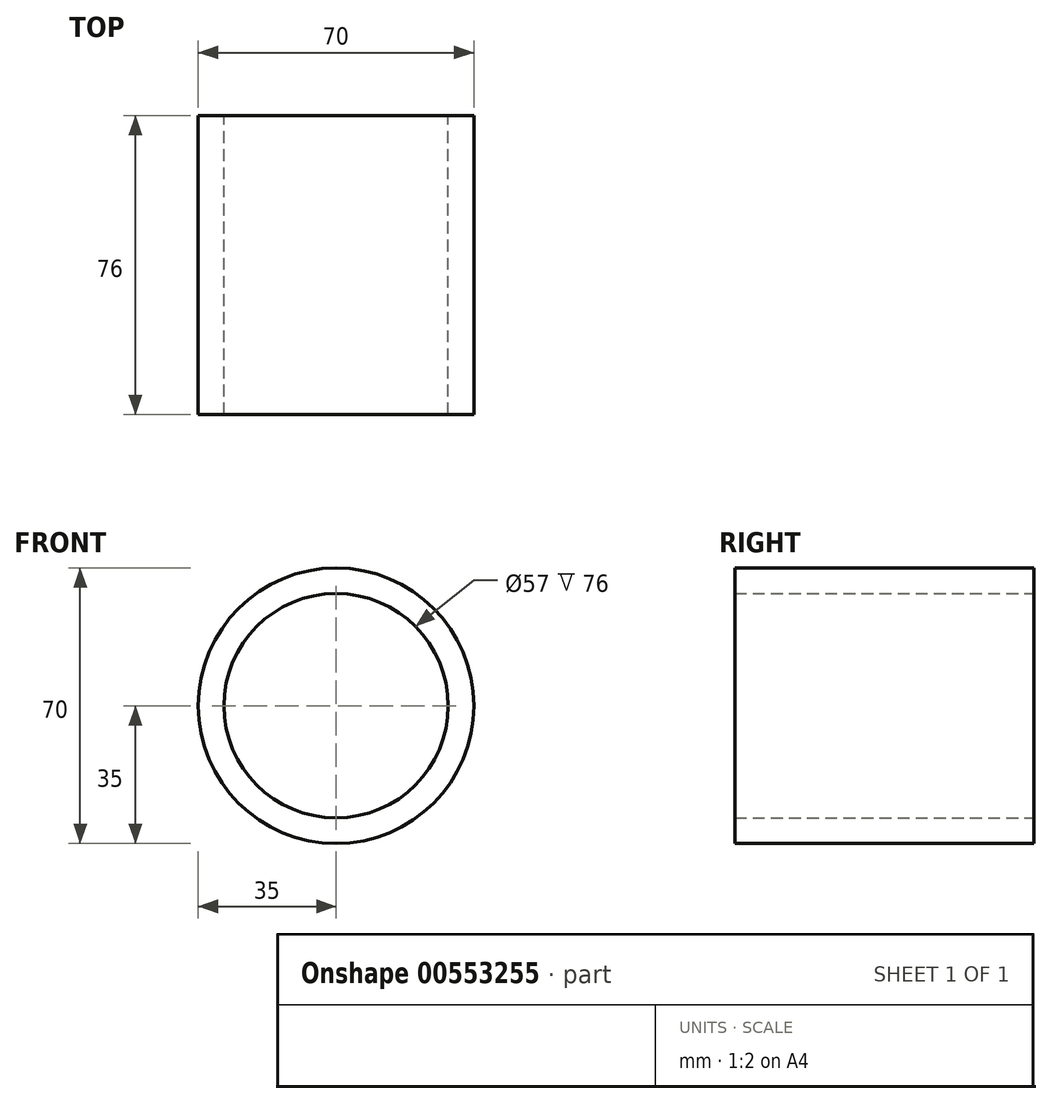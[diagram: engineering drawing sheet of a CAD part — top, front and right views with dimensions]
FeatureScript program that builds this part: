
annotation { "Feature Type Name" : "Feature", "Feature Type Description" : "" }
export const myFeature = defineFeature(function(context is Context, id is Id, definition is map)
    precondition{}
    {
        {
            var Q0;
            Q0=qCreatedBy(makeId("Front.planeOp"),FACE);
            var sketch = newSketch(context, id + "F0", { "sketchPlane" : qUnion([Q0])});
            skCircle(sketch, "E0", {"center": v(0, 0) * mm, "radius": 35 * mm});
            skCircle(sketch, "E1", {"center": v(0, 0) * mm, "radius": 28.5 * mm});
            skSolve(sketch);
        }
        {
            var Q0;
            Q0=makeQuery(id+"F0.imprint","IMPRINT",FACE,{"disambiguationData":[TD([[makeQuery(id+"F0.imprint","IMPRINT",EDGE,{"derivedFrom":sQuery(id+"F0.wireOp",EDGE,"E0")}),1.0]])]});
            extrude(context, id + "F1", {"entities" : qUnion([Q0]), "depth" : 76 * mm, "offsetDistance" : 25 * mm});
        }
    });
